# Revit family: Deca_Monocomando 4 vias_2994.C90_Alta e Baixa Pressão
name_source: partatom
category: Plumbing Fixtures
revit_build: Autodesk Revit Architecture 2012 (Build: 20120126_0600(x64)
units: mm (PartAtom-declared; Revit-internal decimal feet)

## types (1)
- 2994.C90_Cromado CR10
    Aprovado por = Contino/quattroD
    Assembly Code = D2020
    Atendimento ao Cliente = 0800-0117073
    CWFU = 0
    Consumo = Varia com a pressão
    Criado por = Contino/quattroD
    Código = 2994.C90
    Default Elevation = 0 mm  [stored 0 ft]
    Description = Monocomando 4 vias
    Diâmetro Água Fria = 15 mm  [stored 0.0492126 ft]
    Diâmetro Água Quente = 15 mm  [stored 0.0492126 ft]
    Flow Pressure = 0.00 psi
    HWFU = 0
    Informações Complementares = Recomendável com pressão mínima de 6 m.c.a para aquecedor de passagem e de 2 m.c.a para aquecedor de acumulação
    Linha = Unic
    Louça/Metais = Metal
    Manufacturer = Deca
    Material = Deca_Latão Cromado e Plástico de Engenharia
    Model = 2994.C90
    Monocomando = Deca CR10 Cromado Metal
    Norma = ABNT NBR 10283: 2003
    Peso Liquido (Kg) = 2.437
    Pressão = 2 A 40 mca
    Produto = Monocomando 4 vias 1/2 e 3/4 - Alta e Baixa Pressão
    Raio Água Fria = 8 mm  [stored 0.0262467 ft]
    Raio Água Quente = 8 mm  [stored 0.0262467 ft]
    Segmento = Luxo
    URL = www.deca.com.br/produtos
    Variações de COR = Cromado (2994.C90).
    WFU = 0

note: [stored X ft] marks values corroborated as IEEE doubles in the binary element streams (Revit-internal decimal feet)

## geometry (parser evidence)
native form markers: Blend x4, Sweep x1
no freeform markers — native parametric forms only
